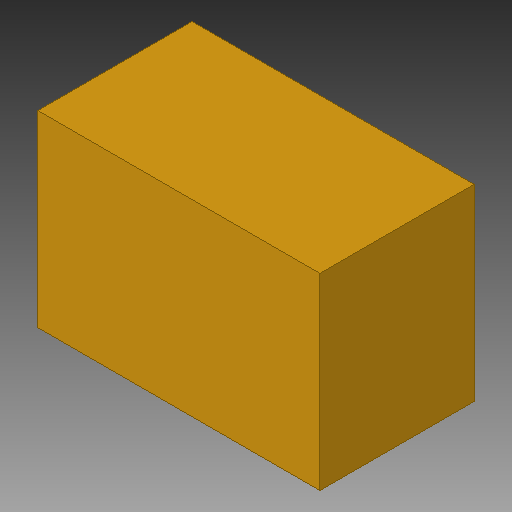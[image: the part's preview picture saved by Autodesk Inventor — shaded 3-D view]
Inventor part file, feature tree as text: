
AUTODESK INVENTOR PART (.ipt)
format: ipt  version: 2018 (Build 220112000, 112)  size: 80,384 bytes
history: native  units: in
note: dims shown in document units (in); Inventor stores cm internally (conversion verified against a paired STEP export)
features: other x1, extrude x1
ambient origin geometry x8: Origin, YZ Plane, XZ Plane, XY Plane, X Axis, Y Axis, Z Axis, Center Point
bodies: Solid1 (feature_tree)
feature tree (2):
  other  "CSMD0805, 1U_32"
  extrude  "Extrusion1"  Depth=0.0394in TaperAngle=0.0deg
